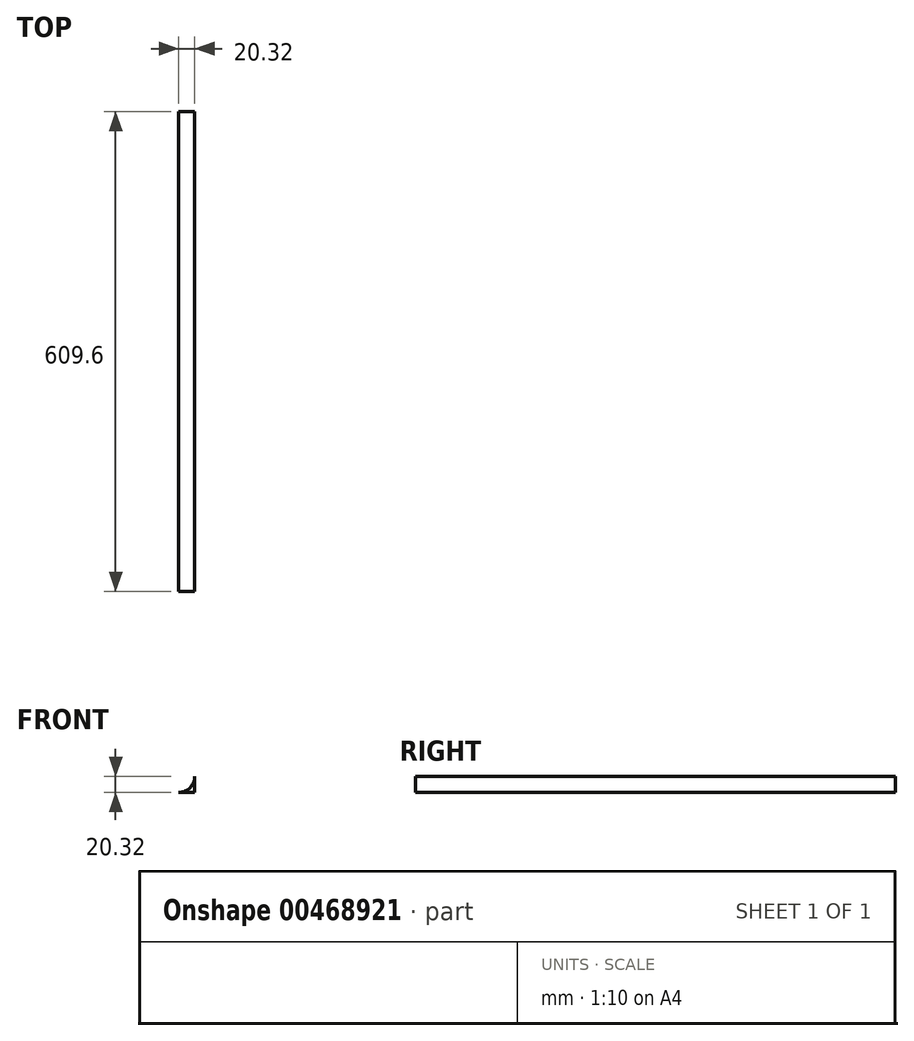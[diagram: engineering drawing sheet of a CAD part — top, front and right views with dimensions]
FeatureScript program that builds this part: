
annotation { "Feature Type Name" : "Feature", "Feature Type Description" : "" }
export const myFeature = defineFeature(function(context is Context, id is Id, definition is map)
    precondition{}
    {
        {
            var Q0;
            Q0=qCreatedBy(makeId("Front.planeOp"),FACE);
            var sketch = newSketch(context, id + "F0", { "sketchPlane" : qUnion([Q0])});
            skLineSegment(sketch, "E0", {"start": v(20.32, 0) * mm, "end": v(20.32, -20.32) * mm});
            skLineSegment(sketch, "E1", {"start": v(20.32, -20.32) * mm, "end": v(0, -20.32) * mm});
            skArc(sketch, "E2", {"start": v(0, -20.32) * mm, "mid": v(14.37, -14.37) * mm, "end": v(20.32, 0) * mm});
            skSolve(sketch);
        }
        {
            var Q0;
            Q0=makeQuery(id+"F0.imprint","IMPRINT",FACE,{"disambiguationData":[TD([[makeQuery(id+"F0.imprint","IMPRINT",EDGE,{"derivedFrom":sQuery(id+"F0.wireOp",EDGE,"E0")}),-1.0]])]});
            extrude(context, id + "F1", {"entities" : qUnion([Q0]), "depth" : 609.6 * mm});
        }
    });
